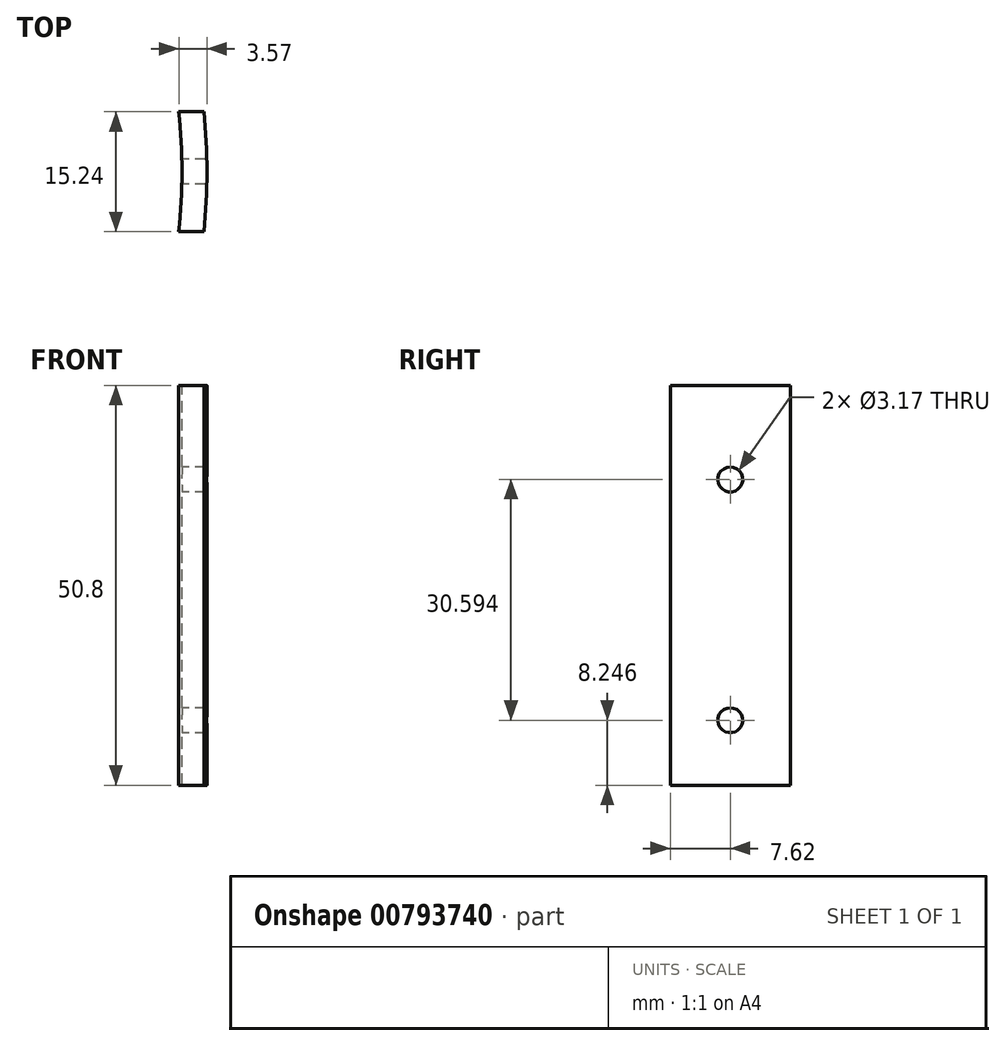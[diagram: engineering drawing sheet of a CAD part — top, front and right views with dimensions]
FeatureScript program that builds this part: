
annotation { "Feature Type Name" : "Feature", "Feature Type Description" : "" }
export const myFeature = defineFeature(function(context is Context, id is Id, definition is map)
    precondition{}
    {
        {
            var Q0;
            Q0=qCreatedBy(makeId("Top.planeOp"),FACE);
            var sketch = newSketch(context, id + "F0", { "sketchPlane" : qUnion([Q0])});
            skCircle(sketch, "E0", {"center": v(0, 0) * mm, "radius": 76.2 * mm});
            skCircle(sketch, "E1", {"center": v(0, 0) * mm, "radius": 73.03 * mm});
            skSolve(sketch);
        }
        {
            var Q0;
            Q0=makeQuery(id+"F0.imprint","IMPRINT",FACE,{"disambiguationData":[TD([[makeQuery(id+"F0.imprint","IMPRINT",EDGE,{"derivedFrom":sQuery(id+"F0.wireOp",EDGE,"E0")}),1.0]])]});
            var Q1;
            Q1=sQuery(id+"F0.wireOp",EDGE,"E0");
            var Q2;
            Q2=sQuery(id+"F0.wireOp",EDGE,"E1");
            extrude(context, id + "F1", {"entities" : qUnion([Q0]), "bodyType" : ToolBodyType.SURFACE, "surfaceEntities" : qUnion([Q1, Q2]), "depth" : 50.8 * mm, "offsetDistance" : 25.4 * mm});
        }
        {
            var Q0;
            Q0=qCreatedBy(makeId("Right.planeOp"),FACE);
            var sketch = newSketch(context, id + "F2", { "sketchPlane" : qUnion([Q0])});
            skLineSegment(sketch, "E2", {"start": v(0, 0) * mm, "end": v(7.62, 0) * mm});
            skLineSegment(sketch, "E3", {"start": v(7.62, 0) * mm, "end": v(7.62, 50.8) * mm});
            skLineSegment(sketch, "E4", {"start": v(7.62, 50.8) * mm, "end": v(-7.62, 50.8) * mm});
            skLineSegment(sketch, "E5", {"start": v(-7.62, 50.8) * mm, "end": v(-7.62, 0) * mm});
            skLineSegment(sketch, "E6", {"start": v(-7.62, 0) * mm, "end": v(0, 0) * mm});
            skCircle(sketch, "E7", {"center": v(0, 8.25) * mm, "radius": 1.59 * mm});
            skCircle(sketch, "E8", {"center": v(0, 38.84) * mm, "radius": 1.59 * mm});
            skSolve(sketch);
        }
        {
            var Q0;
            Q0=makeQuery(id+"F2.imprint","IMPRINT",FACE,{"disambiguationData":[TD([[makeQuery(id+"F2.imprint","IMPRINT",EDGE,{"derivedFrom":sQuery(id+"F2.wireOp",EDGE,"E2")}),1.0]])]});
            var Q1;
            Q1=makeQuery(id+"F1.opExtrude","SWEPT_FACE",FACE,{"disambiguationData":[OSD([sQuery(id+"F0.wireOp",EDGE,"E0")])]});
            extrude(context, id + "F3", {"entities" : qUnion([Q0]), "endBound" : BoundingType.UP_TO_SURFACE, "depth" : 152.4 * mm, "endBoundEntityFace" : qUnion([Q1]), "offsetDistance" : 25.4 * mm});
        }
        {
            var Q0;
            Q0=makeQuery(id+"F3.opExtrude","CAP_FACE",FACE,{"disambiguationData":[OSD([sQuery(id+"F2.wireOp",EDGE,"E2"),sQuery(id+"F2.wireOp",EDGE,"E3"),sQuery(id+"F2.wireOp",EDGE,"E4"),sQuery(id+"F2.wireOp",EDGE,"E5"),sQuery(id+"F2.wireOp",EDGE,"E6"),sQuery(id+"F2.wireOp",EDGE,"E7"),sQuery(id+"F2.wireOp",EDGE,"E8")])],"isStart":true});
            var Q1;
            Q1=makeQuery(id+"F1.opExtrude","SWEPT_FACE",FACE,{"disambiguationData":[OSD([sQuery(id+"F0.wireOp",EDGE,"E1")])]});
            extrude(context, id + "F4", {"entities" : qUnion([Q0]), "operationType" : NewBodyOperationType.REMOVE, "endBound" : BoundingType.UP_TO_SURFACE, "oppositeDirection" : true, "depth" : 25.4 * mm, "endBoundEntityFace" : qUnion([Q1]), "offsetDistance" : 25.4 * mm});
        }
    });
